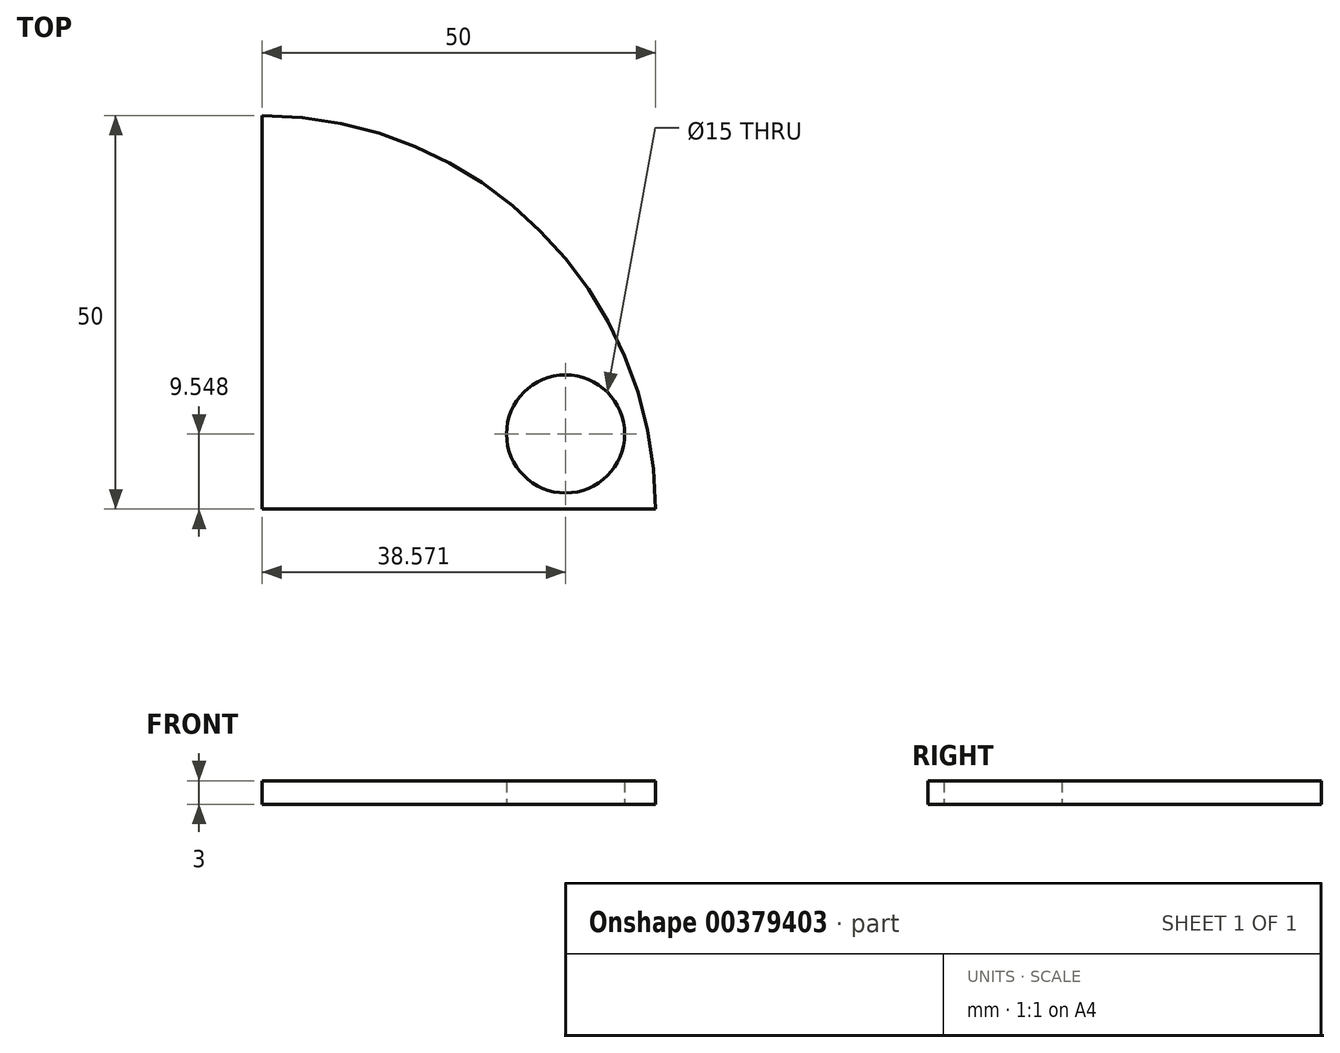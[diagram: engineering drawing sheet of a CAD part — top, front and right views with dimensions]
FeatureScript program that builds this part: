
annotation { "Feature Type Name" : "Feature", "Feature Type Description" : "" }
export const myFeature = defineFeature(function(context is Context, id is Id, definition is map)
    precondition{}
    {
        {
            var Q0;
            Q0=qCreatedBy(makeId("Top.planeOp"),FACE);
            var sketch = newSketch(context, id + "F0", { "sketchPlane" : qUnion([Q0])});
            skLineSegment(sketch, "E0", {"start": v(0, 0) * mm, "end": v(0, 50) * mm});
            skLineSegment(sketch, "E1", {"start": v(0, 0) * mm, "end": v(50, 0) * mm});
            skArc(sketch, "E2", {"start": v(50, 0) * mm, "mid": v(35.36, 35.36) * mm, "end": v(0, 50) * mm});
            skCircle(sketch, "E3", {"center": v(38.57, 9.55) * mm, "radius": 7.5 * mm});
            skSolve(sketch);
        }
        {
            var Q0;
            Q0=makeQuery(id+"F0.imprint","IMPRINT",FACE,{"disambiguationData":[TD([[makeQuery(id+"F0.imprint","IMPRINT",EDGE,{"derivedFrom":sQuery(id+"F0.wireOp",EDGE,"E0")}),-1.0]])]});
            extrude(context, id + "F1", {"entities" : qUnion([Q0]), "depth" : 3 * mm});
        }
    });
